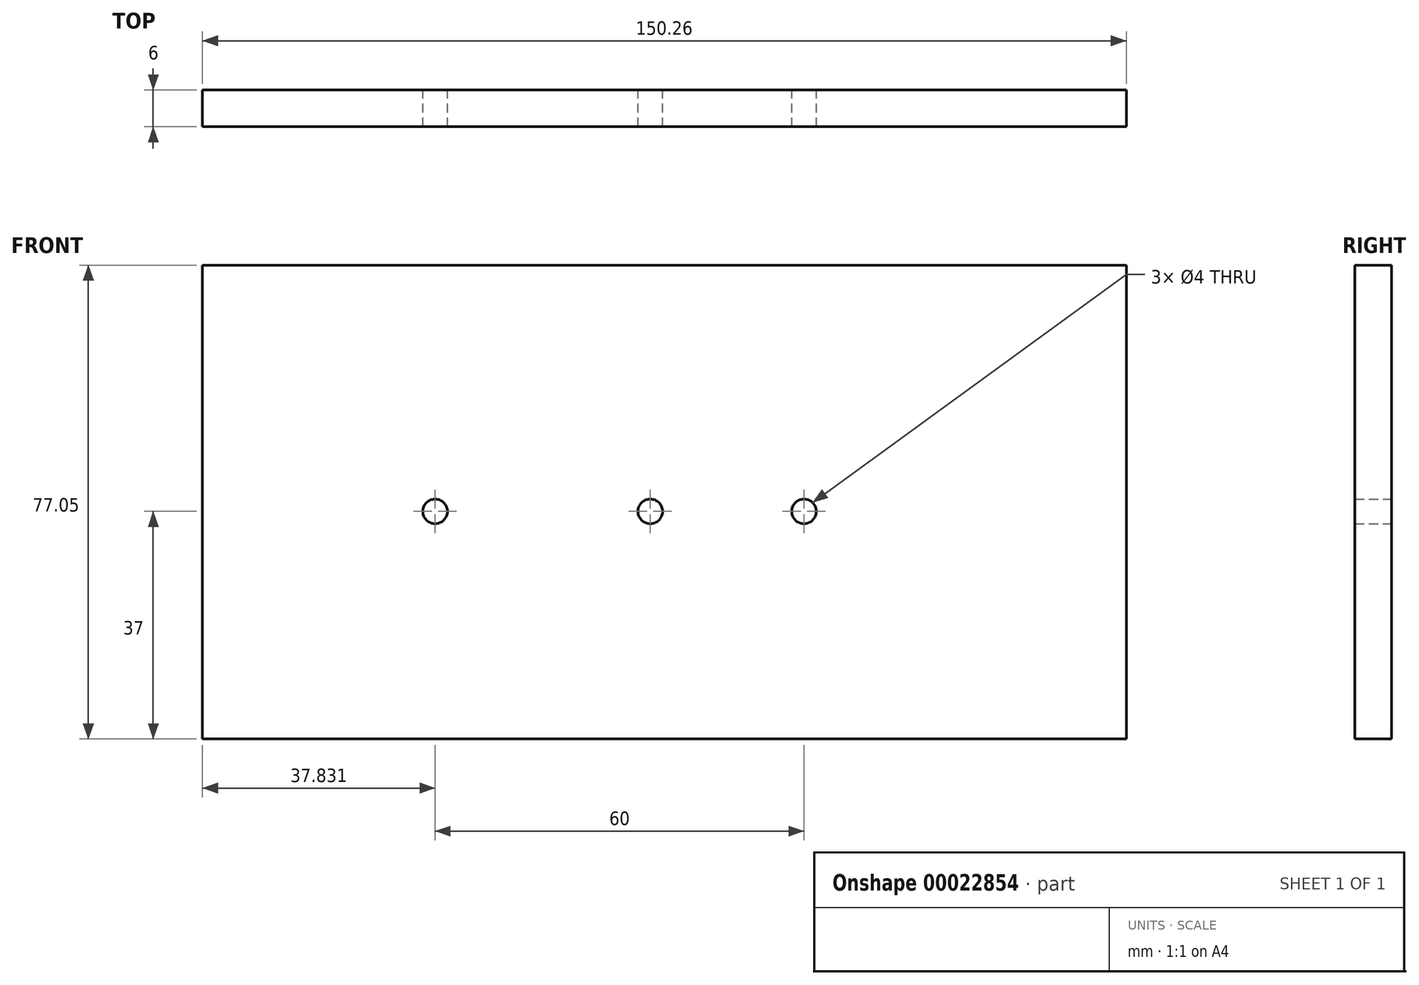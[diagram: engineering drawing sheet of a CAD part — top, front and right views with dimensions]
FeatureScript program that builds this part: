
annotation { "Feature Type Name" : "Feature", "Feature Type Description" : "" }
export const myFeature = defineFeature(function(context is Context, id is Id, definition is map)
    precondition{}
    {
        {
            var Q0;
            Q0=qCreatedBy(makeId("Front.planeOp"),FACE);
            var sketch = newSketch(context, id + "F0", { "sketchPlane" : qUnion([Q0])});
            skLineSegment(sketch, "E0.bottom", {"start": v(-94.2, 47.3) * mm, "end": v(56.07, 47.3) * mm});
            skLineSegment(sketch, "E0.top", {"start": v(-94.2, -29.75) * mm, "end": v(56.07, -29.75) * mm});
            skLineSegment(sketch, "E0.left", {"start": v(-94.2, 47.3) * mm, "end": v(-94.2, -29.75) * mm});
            skLineSegment(sketch, "E0.right", {"start": v(56.07, 47.3) * mm, "end": v(56.07, -29.75) * mm});
            skCircle(sketch, "E1", {"center": v(-56.36, 7.25) * mm, "radius": 2 * mm});
            skCircle(sketch, "E2", {"center": v(-21.36, 7.25) * mm, "radius": 2 * mm});
            skCircle(sketch, "E3", {"center": v(3.64, 7.25) * mm, "radius": 2 * mm});
            skSolve(sketch);
        }
        {
            var Q0;
            Q0=makeQuery(id+"F0.imprint","IMPRINT",FACE,{"disambiguationData":[TD([[makeQuery(id+"F0.imprint","IMPRINT",EDGE,{"derivedFrom":sQuery(id+"F0.wireOp",EDGE,"E0.bottom")}),-1.0]])]});
            extrude(context, id + "F1", {"entities" : qUnion([Q0]), "depth" : 6 * mm});
        }
    });
